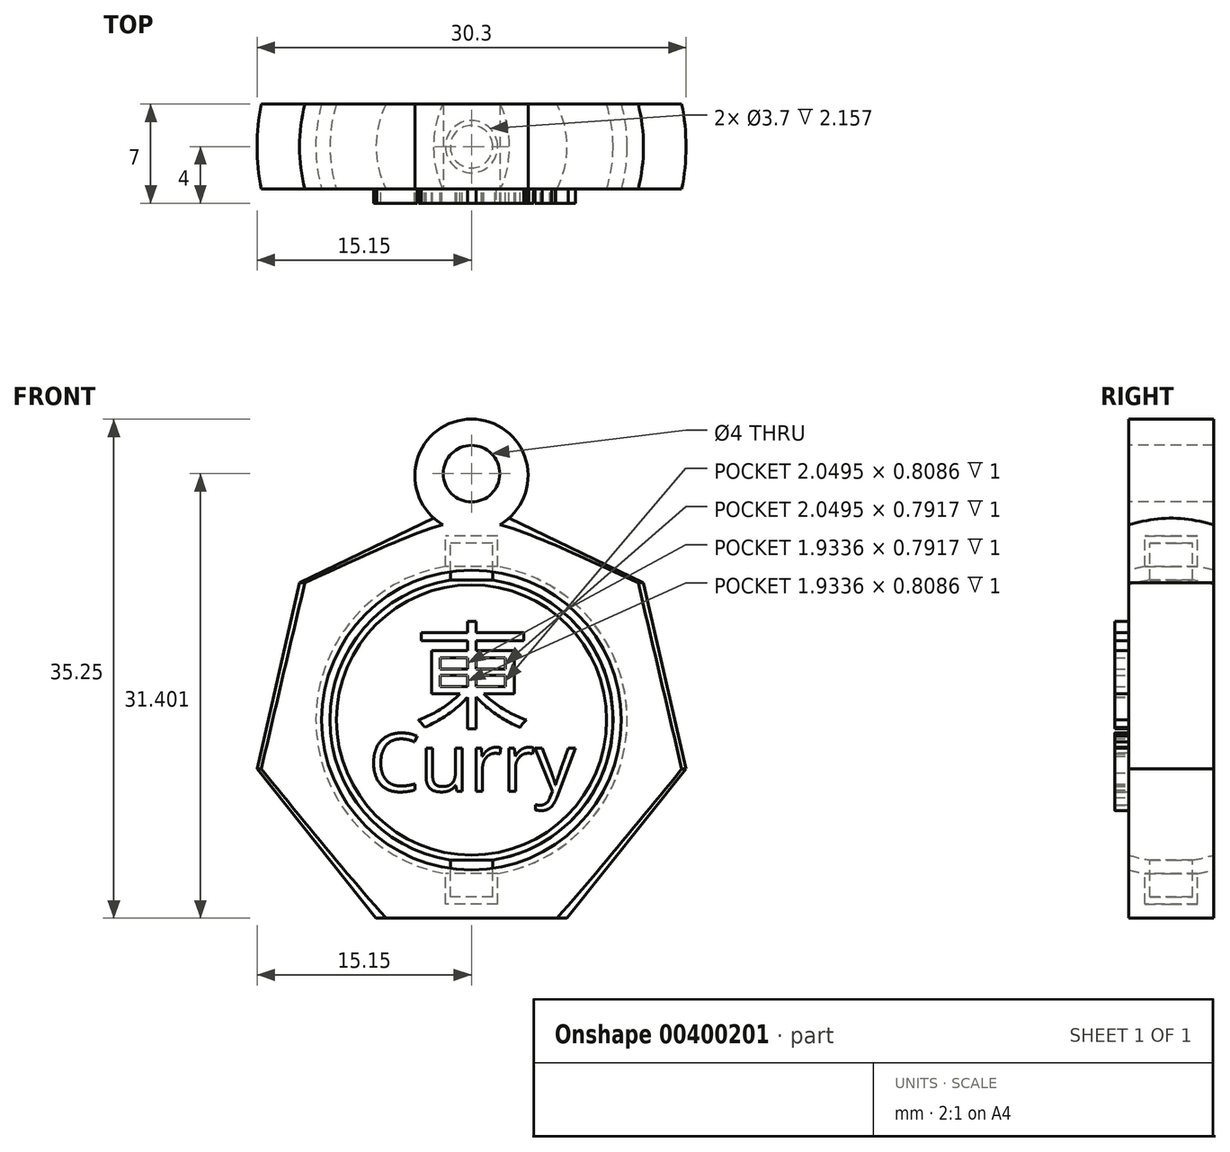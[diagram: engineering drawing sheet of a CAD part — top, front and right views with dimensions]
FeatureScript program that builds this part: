
annotation { "Feature Type Name" : "Feature", "Feature Type Description" : "" }
export const myFeature = defineFeature(function(context is Context, id is Id, definition is map)
    precondition{}
    {
        {
            var Q0;
            Q0=qCreatedBy(makeId("Front.planeOp"),FACE);
            var sketch = newSketch(context, id + "F0", { "sketchPlane" : qUnion([Q0])});
            skLineSegment(sketch, "E0.bottom", {"start": v(1.85, -13) * mm, "end": v(-1.85, -13) * mm});
            skLineSegment(sketch, "E0.top", {"start": v(1.85, 13) * mm, "end": v(-1.85, 13) * mm});
            skLineSegment(sketch, "E0.left", {"start": v(1.85, -13) * mm, "end": v(1.85, 13) * mm});
            skLineSegment(sketch, "E0.right", {"start": v(-1.85, -13) * mm, "end": v(-1.85, 13) * mm});
            skPoint(sketch, "E0.middle", {"position": v(0, 0) * mm});
            skLineSegment(sketch, "E1.bottom", {"start": v(1.5, -12.5) * mm, "end": v(-1.5, -12.5) * mm});
            skLineSegment(sketch, "E1.top", {"start": v(1.5, 12.5) * mm, "end": v(-1.5, 12.5) * mm});
            skLineSegment(sketch, "E1.left", {"start": v(1.5, -12.5) * mm, "end": v(1.5, 12.5) * mm});
            skLineSegment(sketch, "E1.right", {"start": v(-1.5, -12.5) * mm, "end": v(-1.5, 12.5) * mm});
            skCircle(sketch, "E2", {"center": v(0, 0) * mm, "radius": 10 * mm});
            skCircle(sketch, "E3", {"center": v(0, 0) * mm, "radius": 11 * mm});
            skCircle(sketch, "E4.cCircle", {"center": v(0, 0) * mm, "radius": 14 * mm, "construction": true});
            skLineSegment(sketch, "E4.0", {"start": v(15.15, -3.46) * mm, "end": v(6.74, -14) * mm});
            skLineSegment(sketch, "E4.1", {"start": v(6.74, -14) * mm, "end": v(-6.74, -14) * mm});
            skLineSegment(sketch, "E4.2", {"start": v(-6.74, -14) * mm, "end": v(-15.15, -3.46) * mm});
            skLineSegment(sketch, "E4.3", {"start": v(-15.15, -3.46) * mm, "end": v(-12.15, 9.69) * mm});
            skLineSegment(sketch, "E4.4", {"start": v(-12.15, 9.69) * mm, "end": v(0, 15.54) * mm});
            skLineSegment(sketch, "E4.5", {"start": v(0, 15.54) * mm, "end": v(12.15, 9.69) * mm});
            skLineSegment(sketch, "E4.6", {"start": v(12.15, 9.69) * mm, "end": v(15.15, -3.46) * mm});
            skPoint(sketch, "E4.0.midPoint", {"position": v(10.95, -8.73) * mm});
            skSolve(sketch);
        }
        {
            var Q0;
            Q0=qCreatedBy(makeId("Front.planeOp"),FACE);
            var sketch = newSketch(context, id + "F1", { "sketchPlane" : qUnion([Q0])});
            skLineSegment(sketch, "E5.0", {"start": v(-6.74, -14) * mm, "end": v(-15.15, -3.46) * mm});
            skLineSegment(sketch, "E5.1", {"start": v(12.15, 9.69) * mm, "end": v(15.15, -3.46) * mm});
            skLineSegment(sketch, "E5.2", {"start": v(-15.15, -3.46) * mm, "end": v(-12.15, 9.69) * mm});
            skLineSegment(sketch, "E5.3", {"start": v(-12.15, 9.69) * mm, "end": v(0, 15.54) * mm});
            skLineSegment(sketch, "E5.4", {"start": v(1.85, -13) * mm, "end": v(-1.85, -13) * mm});
            skLineSegment(sketch, "E5.5", {"start": v(1.85, 13) * mm, "end": v(-1.85, 13) * mm});
            skLineSegment(sketch, "E5.6", {"start": v(1.85, -13) * mm, "end": v(1.85, -10.84) * mm});
            skLineSegment(sketch, "E5.7", {"start": v(-1.85, -13) * mm, "end": v(-1.85, -10.84) * mm});
            skLineSegment(sketch, "E5.8", {"start": v(1.5, -12.5) * mm, "end": v(-1.5, -12.5) * mm});
            skLineSegment(sketch, "E5.9", {"start": v(1.5, 12.5) * mm, "end": v(-1.5, 12.5) * mm});
            skLineSegment(sketch, "E5.10", {"start": v(1.5, -12.5) * mm, "end": v(1.5, -9.89) * mm});
            skLineSegment(sketch, "E5.11", {"start": v(-1.5, -12.5) * mm, "end": v(-1.5, -9.89) * mm});
            skArc(sketch, "E5.12", {"start": v(-1.5, 9.89) * mm, "mid": v(-10, 0) * mm, "end": v(-1.5, -9.89) * mm});
            skArc(sketch, "E5.13", {"start": v(-1.85, 10.84) * mm, "mid": v(-11, 0) * mm, "end": v(-1.85, -10.84) * mm});
            skLineSegment(sketch, "E5.15", {"start": v(15.15, -3.46) * mm, "end": v(6.74, -14) * mm});
            skLineSegment(sketch, "E5.16", {"start": v(6.74, -14) * mm, "end": v(-6.74, -14) * mm});
            skLineSegment(sketch, "E5.17", {"start": v(0, 15.54) * mm, "end": v(12.15, 9.69) * mm});
            skLineSegment(sketch, "E6.trimOffspring", {"start": v(-1.5, 9.89) * mm, "end": v(-1.5, 12.5) * mm});
            skLineSegment(sketch, "E7.trimOffspring", {"start": v(-1.85, 10.84) * mm, "end": v(-1.85, 13) * mm});
            skLineSegment(sketch, "E8.trimOffspring", {"start": v(1.5, 9.89) * mm, "end": v(1.5, 12.5) * mm});
            skLineSegment(sketch, "E9.trimOffspring", {"start": v(1.85, 10.84) * mm, "end": v(1.85, 13) * mm});
            skArc(sketch, "E10.trimOffspring", {"start": v(1.5, -9.89) * mm, "mid": v(10, 0) * mm, "end": v(1.5, 9.89) * mm});
            skArc(sketch, "E11.trimOffspring", {"start": v(1.85, -10.84) * mm, "mid": v(11, 0) * mm, "end": v(1.85, 10.84) * mm});
            skSolve(sketch);
        }
        {
            var Q0;
            Q0=qCreatedBy(makeId("Front.planeOp"),FACE);
            var sketch = newSketch(context, id + "F2", { "sketchPlane" : qUnion([Q0])});
            skLineSegment(sketch, "E12.0", {"start": v(-6.74, -14) * mm, "end": v(-15.15, -3.46) * mm});
            skLineSegment(sketch, "E12.1", {"start": v(12.15, 9.69) * mm, "end": v(15.15, -3.46) * mm});
            skLineSegment(sketch, "E12.2", {"start": v(-15.15, -3.46) * mm, "end": v(-12.15, 9.69) * mm});
            skLineSegment(sketch, "E12.3", {"start": v(-12.15, 9.69) * mm, "end": v(0, 15.54) * mm});
            skLineSegment(sketch, "E12.4", {"start": v(1.85, -13) * mm, "end": v(-1.85, -13) * mm});
            skLineSegment(sketch, "E12.5", {"start": v(1.85, 13) * mm, "end": v(-1.85, 13) * mm});
            skLineSegment(sketch, "E12.6", {"start": v(1.85, -13) * mm, "end": v(1.85, -10.84) * mm});
            skLineSegment(sketch, "E12.7", {"start": v(-1.85, -13) * mm, "end": v(-1.85, -10.84) * mm});
            skLineSegment(sketch, "E12.8", {"start": v(1.5, -12.5) * mm, "end": v(-1.5, -12.5) * mm});
            skLineSegment(sketch, "E12.9", {"start": v(1.5, 12.5) * mm, "end": v(-1.5, 12.5) * mm});
            skLineSegment(sketch, "E12.10", {"start": v(1.5, -12.5) * mm, "end": v(1.5, -9.89) * mm});
            skLineSegment(sketch, "E12.11", {"start": v(-1.5, -12.5) * mm, "end": v(-1.5, -9.89) * mm});
            skArc(sketch, "E12.12", {"start": v(-1.5, 9.89) * mm, "mid": v(-10, 0) * mm, "end": v(-1.5, -9.89) * mm});
            skArc(sketch, "E12.13", {"start": v(-1.85, 10.84) * mm, "mid": v(-11, 0) * mm, "end": v(-1.85, -10.84) * mm});
            skLineSegment(sketch, "E12.14", {"start": v(15.15, -3.46) * mm, "end": v(6.74, -14) * mm});
            skLineSegment(sketch, "E12.15", {"start": v(6.74, -14) * mm, "end": v(-6.74, -14) * mm});
            skLineSegment(sketch, "E12.16", {"start": v(0, 15.54) * mm, "end": v(12.15, 9.69) * mm});
            skLineSegment(sketch, "E12.17", {"start": v(-1.5, 9.89) * mm, "end": v(-1.5, 12.5) * mm});
            skLineSegment(sketch, "E12.18", {"start": v(-1.85, 10.84) * mm, "end": v(-1.85, 13) * mm});
            skLineSegment(sketch, "E12.19", {"start": v(1.5, 9.89) * mm, "end": v(1.5, 12.5) * mm});
            skLineSegment(sketch, "E12.20", {"start": v(1.85, 10.84) * mm, "end": v(1.85, 13) * mm});
            skArc(sketch, "E12.21", {"start": v(1.5, -9.89) * mm, "mid": v(10, 0) * mm, "end": v(1.5, 9.89) * mm});
            skArc(sketch, "E12.22", {"start": v(1.85, -10.84) * mm, "mid": v(11, 0) * mm, "end": v(1.85, 10.84) * mm});
            skLineSegment(sketch, "E13", {"start": v(0, 15.54) * mm, "end": v(0, -14) * mm});
            skSolve(sketch);
        }
        {
            var Q0;
            Q0=qCreatedBy(makeId("Front.planeOp"),FACE);
            var sketch = newSketch(context, id + "F3", { "sketchPlane" : qUnion([Q0])});
            skLineSegment(sketch, "E14.1", {"start": v(12.15, 9.69) * mm, "end": v(15.15, -3.46) * mm});
            skLineSegment(sketch, "E14.4", {"start": v(1.85, -13) * mm, "end": v(0, -13) * mm});
            skLineSegment(sketch, "E14.5", {"start": v(1.85, 13) * mm, "end": v(0, 13) * mm});
            skLineSegment(sketch, "E14.6", {"start": v(1.85, -13) * mm, "end": v(1.85, -10.84) * mm});
            skLineSegment(sketch, "E14.8", {"start": v(1.5, -12.5) * mm, "end": v(0, -12.5) * mm});
            skLineSegment(sketch, "E14.9", {"start": v(1.5, 12.5) * mm, "end": v(0, 12.5) * mm});
            skLineSegment(sketch, "E14.10", {"start": v(1.5, -12.5) * mm, "end": v(1.5, -9.89) * mm});
            skLineSegment(sketch, "E14.14", {"start": v(15.15, -3.46) * mm, "end": v(6.74, -14) * mm});
            skLineSegment(sketch, "E14.15", {"start": v(6.74, -14) * mm, "end": v(0, -14) * mm});
            skLineSegment(sketch, "E14.16", {"start": v(0, 15.54) * mm, "end": v(12.15, 9.69) * mm});
            skLineSegment(sketch, "E14.19", {"start": v(1.5, 9.89) * mm, "end": v(1.5, 12.5) * mm});
            skLineSegment(sketch, "E14.20", {"start": v(1.85, 10.84) * mm, "end": v(1.85, 13) * mm});
            skArc(sketch, "E14.21", {"start": v(1.5, -9.89) * mm, "mid": v(10, 0) * mm, "end": v(1.5, 9.89) * mm});
            skArc(sketch, "E14.22", {"start": v(1.85, -10.84) * mm, "mid": v(11, 0) * mm, "end": v(1.85, 10.84) * mm});
            skLineSegment(sketch, "E14.23", {"start": v(0, 15.54) * mm, "end": v(0, 13) * mm});
            skPoint(sketch, "E14.3.end.orphan", {"position": v(0, 15.54) * mm});
            skPoint(sketch, "E14.3.start.orphan", {"position": v(-12.15, 9.69) * mm});
            skPoint(sketch, "E14.17.end.orphan", {"position": v(-1.5, 12.5) * mm});
            skPoint(sketch, "E14.17.start.orphan", {"position": v(-1.5, 9.89) * mm});
            skPoint(sketch, "E14.18.end.orphan", {"position": v(-1.85, 13) * mm});
            skPoint(sketch, "E14.18.start.orphan", {"position": v(-1.85, 10.84) * mm});
            skPoint(sketch, "E14.13.end.orphan", {"position": v(-1.85, -10.84) * mm});
            skPoint(sketch, "E14.13.start.orphan", {"position": v(-1.85, 10.84) * mm});
            skPoint(sketch, "E14.12.end.orphan", {"position": v(-1.5, -9.89) * mm});
            skPoint(sketch, "E14.12.start.orphan", {"position": v(-1.5, 9.89) * mm});
            skPoint(sketch, "E14.2.end.orphan", {"position": v(-12.15, 9.69) * mm});
            skPoint(sketch, "E14.2.start.orphan", {"position": v(-15.15, -3.46) * mm});
            skLineSegment(sketch, "E15.trimOffspring", {"start": v(0, 12.5) * mm, "end": v(0, -12.5) * mm});
            skPoint(sketch, "E14.0.end.orphan", {"position": v(-15.15, -3.46) * mm});
            skPoint(sketch, "E14.0.start.orphan", {"position": v(-6.74, -14) * mm});
            skPoint(sketch, "E14.11.end.orphan", {"position": v(-1.5, -9.89) * mm});
            skPoint(sketch, "E14.11.start.orphan", {"position": v(-1.5, -12.5) * mm});
            skPoint(sketch, "E14.7.end.orphan", {"position": v(-1.85, -10.84) * mm});
            skPoint(sketch, "E14.7.start.orphan", {"position": v(-1.85, -13) * mm});
            skLineSegment(sketch, "E16.trimOffspring", {"start": v(0, -13) * mm, "end": v(0, -14) * mm});
            skSolve(sketch);
        }
        {
            var Q0;
            Q0 = qSketchRegion(id + "F3", true);
            var Q1;
            Q1=sQuery(id+"F3.wireOp",EDGE,"E15.trimOffspring");
            revolve(context, id + "F4", {"entities" : qUnion([Q0]), "axis" : qUnion([Q1]), "revolveType" : RevolveType.FULL, "surfaceOperationType" : NewSurfaceOperationType.NEW});
        }
        {
            var Q0;
            Q0=qCreatedBy(makeId("Right.planeOp"),FACE);
            var sketch = newSketch(context, id + "F5", { "sketchPlane" : qUnion([Q0])});
            skLineSegment(sketch, "E17.bottom", {"start": v(3, 20.08) * mm, "end": v(25.6, 20.08) * mm});
            skLineSegment(sketch, "E17.top", {"start": v(3, -19.17) * mm, "end": v(25.6, -19.17) * mm});
            skLineSegment(sketch, "E17.left", {"start": v(3, 20.08) * mm, "end": v(3, -19.17) * mm});
            skLineSegment(sketch, "E17.right", {"start": v(25.6, 20.08) * mm, "end": v(25.6, -19.17) * mm});
            skLineSegment(sketch, "E18.MirrorCS", {"start": v(-3, 20.08) * mm, "end": v(-25.6, 20.08) * mm});
            skLineSegment(sketch, "E19.MirrorCS", {"start": v(-3, -19.17) * mm, "end": v(-25.6, -19.17) * mm});
            skLineSegment(sketch, "E20.MirrorCS", {"start": v(-3, 20.08) * mm, "end": v(-3, -19.17) * mm});
            skLineSegment(sketch, "E21.MirrorCS", {"start": v(-25.6, 20.08) * mm, "end": v(-25.6, -19.17) * mm});
            skSolve(sketch);
        }
        {
            var Q0;
            Q0 = qSketchRegion(id + "F5", true);
            extrude(context, id + "F6", {"entities" : qUnion([Q0]), "operationType" : NewBodyOperationType.REMOVE, "endBound" : BoundingType.SYMMETRIC, "oppositeDirection" : true, "depth" : 60 * mm});
        }
        {
            var Q0;
            Q0=qCreatedBy(makeId("Front.planeOp"),FACE);
            var sketch = newSketch(context, id + "F7", { "sketchPlane" : qUnion([Q0])});
            skText(sketch, "E22", { "text": "東", "fontName": "NotoSansCJKjp-Regular.otf"});
            const initialGuessF7  = {"E22": [-0.00412, 0, 1, 0, 0.006]};
            skSetInitialGuess(sketch, initialGuessF7);
            skSolve(sketch);
        }
        {
            var Q0;
            Q0 = qSketchRegion(id + "F7", true);
            extrude(context, id + "F8", {"entities" : qUnion([Q0]), "operationType" : NewBodyOperationType.ADD, "depth" : 4 * mm});
        }
        {
            var Q0;
            Q0=qCreatedBy(makeId("Front.planeOp"),FACE);
            var sketch = newSketch(context, id + "F9", { "sketchPlane" : qUnion([Q0])});
            skText(sketch, "E23", { "text": "Curry", "fontName": "OpenSans-Regular.ttf"});
            const initialGuessF9  = {"E23": [-0.00726, -0.00503, 1, 0, 0.0041]};
            skSetInitialGuess(sketch, initialGuessF9);
            skSolve(sketch);
        }
        {
            var Q0;
            Q0 = qSketchRegion(id + "F9", true);
            extrude(context, id + "F10", {"entities" : qUnion([Q0]), "operationType" : NewBodyOperationType.ADD, "depth" : 4 * mm});
        }
        {
            var Q0;
            Q0=qCreatedBy(makeId("Front.planeOp"),FACE);
            var sketch = newSketch(context, id + "F11", { "sketchPlane" : qUnion([Q0])});
            skCircle(sketch, "E24", {"center": v(0, 17.25) * mm, "radius": 4 * mm});
            skSolve(sketch);
        }
        {
            var Q0;
            Q0 = qSketchRegion(id + "F11", true);
            extrude(context, id + "F12", {"entities" : qUnion([Q0]), "operationType" : NewBodyOperationType.ADD, "endBound" : BoundingType.SYMMETRIC, "depth" : 6 * mm});
        }
        {
            var Q0;
            Q0=qCreatedBy(makeId("Front.planeOp"),FACE);
            var sketch = newSketch(context, id + "F13", { "sketchPlane" : qUnion([Q0])});
            skCircle(sketch, "E25", {"center": v(0, 17.4) * mm, "radius": 2 * mm});
            skSolve(sketch);
        }
        {
            var Q0;
            Q0 = qSketchRegion(id + "F13", true);
            extrude(context, id + "F14", {"entities" : qUnion([Q0]), "operationType" : NewBodyOperationType.REMOVE, "endBound" : BoundingType.SYMMETRIC, "oppositeDirection" : true, "depth" : 25 * mm});
        }
    });
